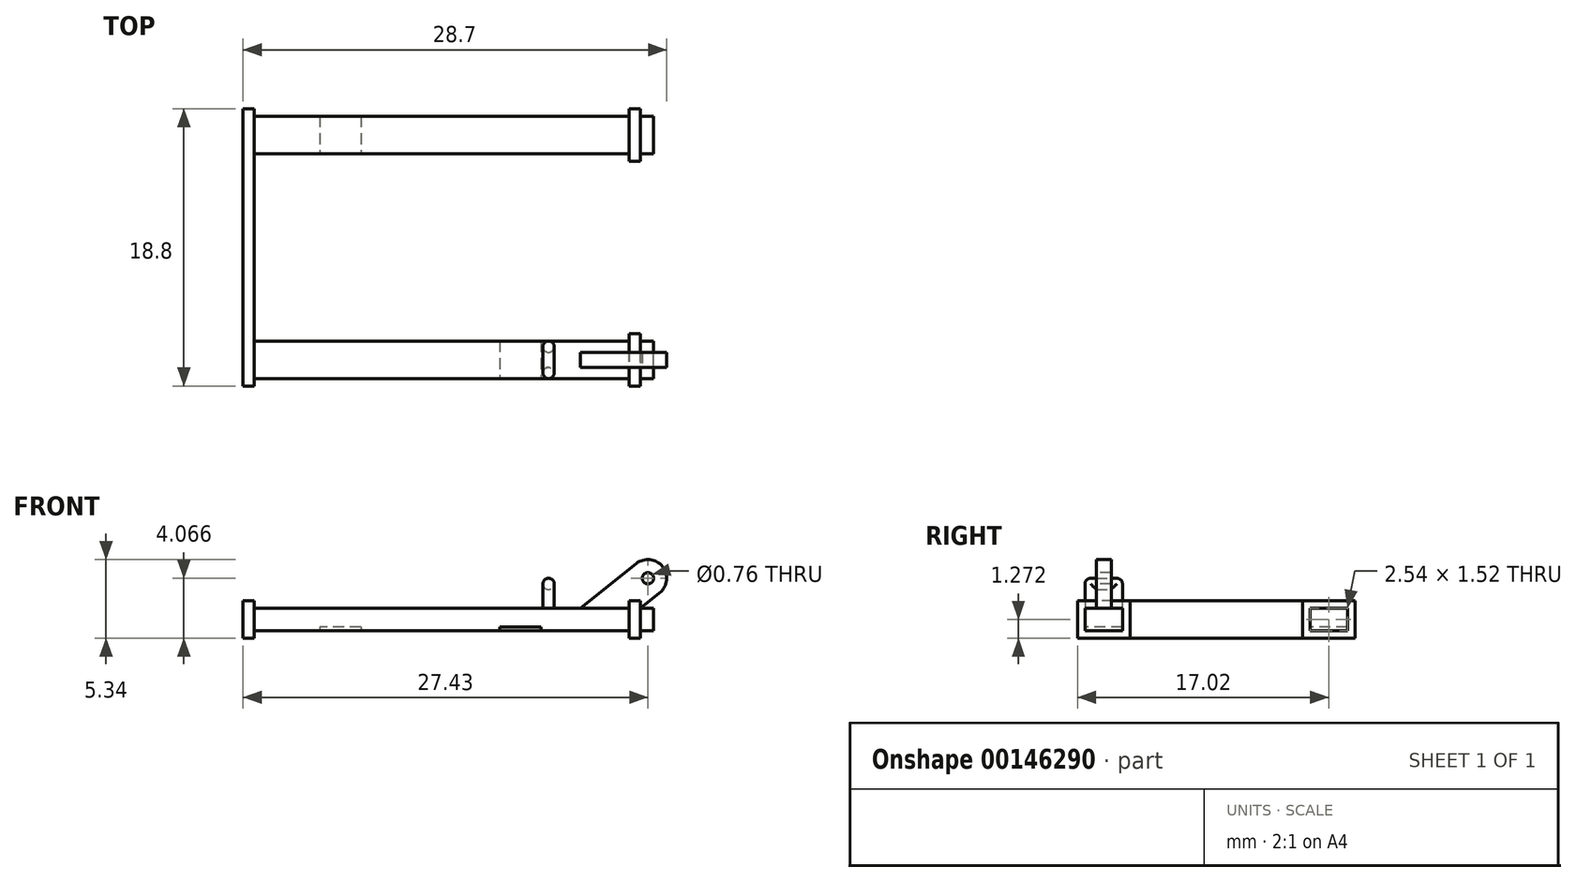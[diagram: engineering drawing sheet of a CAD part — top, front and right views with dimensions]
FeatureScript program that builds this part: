
annotation { "Feature Type Name" : "Feature", "Feature Type Description" : "" }
export const myFeature = defineFeature(function(context is Context, id is Id, definition is map)
    precondition{}
    {
        {
            var Q0;
            Q0=qCreatedBy(makeId("Top.planeOp"),FACE);
            var sketch = newSketch(context, id + "F0", { "sketchPlane" : qUnion([Q0])});
            skLineSegment(sketch, "E0.bottom", {"start": v(-12.7, 2.54) * mm, "end": v(12.7, 2.54) * mm});
            skLineSegment(sketch, "E0.top", {"start": v(-12.7, 0) * mm, "end": v(12.7, 0) * mm});
            skLineSegment(sketch, "E0.left", {"start": v(-12.7, 2.54) * mm, "end": v(-12.7, 0) * mm});
            skLineSegment(sketch, "E0.right", {"start": v(12.7, 2.54) * mm, "end": v(12.7, 0) * mm});
            skLineSegment(sketch, "E1.bottom", {"start": v(-12.7, 15.24) * mm, "end": v(12.7, 15.24) * mm});
            skLineSegment(sketch, "E1.top", {"start": v(-12.7, 17.78) * mm, "end": v(12.7, 17.78) * mm});
            skLineSegment(sketch, "E1.left", {"start": v(-12.7, 15.24) * mm, "end": v(-12.7, 17.78) * mm});
            skLineSegment(sketch, "E1.right", {"start": v(12.7, 15.24) * mm, "end": v(12.7, 17.78) * mm});
            skLineSegment(sketch, "E2.bottom", {"start": v(12.7, 18.29) * mm, "end": v(13.46, 18.29) * mm});
            skLineSegment(sketch, "E2.top", {"start": v(12.7, 14.73) * mm, "end": v(13.46, 14.73) * mm});
            skLineSegment(sketch, "E2.left", {"start": v(12.7, 18.29) * mm, "end": v(12.7, 14.73) * mm});
            skLineSegment(sketch, "E2.right", {"start": v(13.46, 18.29) * mm, "end": v(13.46, 14.73) * mm});
            skLineSegment(sketch, "E3.bottom", {"start": v(12.7, 3.05) * mm, "end": v(13.46, 3.05) * mm});
            skLineSegment(sketch, "E3.top", {"start": v(12.7, -0.5) * mm, "end": v(13.46, -0.5) * mm});
            skLineSegment(sketch, "E3.left", {"start": v(12.7, 3.05) * mm, "end": v(12.7, -0.5) * mm});
            skLineSegment(sketch, "E3.right", {"start": v(13.46, 3.05) * mm, "end": v(13.46, -0.5) * mm});
            skLineSegment(sketch, "E4.bottom", {"start": v(-12.7, 18.29) * mm, "end": v(-13.46, 18.29) * mm});
            skLineSegment(sketch, "E4.top", {"start": v(-12.7, -0.5) * mm, "end": v(-13.46, -0.5) * mm});
            skLineSegment(sketch, "E4.left", {"start": v(-12.7, 18.29) * mm, "end": v(-12.7, -0.5) * mm});
            skLineSegment(sketch, "E4.right", {"start": v(-13.46, 18.29) * mm, "end": v(-13.46, -0.5) * mm});
            skLineSegment(sketch, "E5.bottom", {"start": v(7.62, 15.24) * mm, "end": v(9.14, 15.24) * mm});
            skLineSegment(sketch, "E5.top", {"start": v(7.62, 2.54) * mm, "end": v(9.14, 2.54) * mm});
            skLineSegment(sketch, "E5.left", {"start": v(7.62, 15.24) * mm, "end": v(7.62, 2.54) * mm});
            skLineSegment(sketch, "E5.right", {"start": v(9.14, 15.24) * mm, "end": v(9.14, 2.54) * mm});
            skSolve(sketch);
        }
        {
            var Q0;
            {var subQ3=sQuery(id+"F0.wireOp",EDGE,"E1.top");Q0=makeQuery(id+"F0.imprint","IMPRINT",FACE,{"disambiguationData":[TD([[makeQuery(id+"F0.imprint","IMPRINT",EDGE,{"derivedFrom":subQ3}),-1.0]])]});}
            var Q1;
            {var subQ3=sQuery(id+"F0.wireOp",EDGE,"E4.bottom");Q1=makeQuery(id+"F0.imprint","IMPRINT",FACE,{"disambiguationData":[TD([[makeQuery(id+"F0.imprint","IMPRINT",EDGE,{"derivedFrom":subQ3}),1.0]])]});}
            var Q2;
            {var subQ3=sQuery(id+"F0.wireOp",EDGE,"E0.top");Q2=makeQuery(id+"F0.imprint","IMPRINT",FACE,{"disambiguationData":[TD([[makeQuery(id+"F0.imprint","IMPRINT",EDGE,{"derivedFrom":subQ3}),1.0]])]});}
            var Q3;
            Q3=makeQuery(id+"F0.imprint","IMPRINT",FACE,{"disambiguationData":[TD([[makeQuery(id+"F0.imprint","IMPRINT",EDGE,{"derivedFrom":sQuery(id+"F0.wireOp",EDGE,"E5.bottom")}),-1.0]])]});
            var Q4;
            {var subQ3=sQuery(id+"F0.wireOp",EDGE,"E3.bottom");Q4=makeQuery(id+"F0.imprint","IMPRINT",FACE,{"disambiguationData":[TD([[makeQuery(id+"F0.imprint","IMPRINT",EDGE,{"derivedFrom":subQ3}),-1.0]])]});}
            var Q5;
            {var subQ3=sQuery(id+"F0.wireOp",EDGE,"E2.bottom");Q5=makeQuery(id+"F0.imprint","IMPRINT",FACE,{"disambiguationData":[TD([[makeQuery(id+"F0.imprint","IMPRINT",EDGE,{"derivedFrom":subQ3}),-1.0]])]});}
            extrude(context, id + "F1", {"entities" : qUnion([Q0, Q1, Q2, Q3, Q4, Q5]), "depth" : 1.52 * mm});
        }
        {
            var Q0;
            Q0=makeQuery(id+"F1.opExtrude","CAP_FACE",FACE,{"disambiguationData":[OSD([sQuery(id+"F0.wireOp",EDGE,"E0.bottom"),sQuery(id+"F0.wireOp",EDGE,"E0.top"),sQuery(id+"F0.wireOp",EDGE,"E1.bottom"),sQuery(id+"F0.wireOp",EDGE,"E1.top"),sQuery(id+"F0.wireOp",EDGE,"E2.bottom"),sQuery(id+"F0.wireOp",EDGE,"E2.top"),sQuery(id+"F0.wireOp",EDGE,"E2.left"),sQuery(id+"F0.wireOp",EDGE,"E2.right"),sQuery(id+"F0.wireOp",EDGE,"E3.bottom"),sQuery(id+"F0.wireOp",EDGE,"E3.top"),sQuery(id+"F0.wireOp",EDGE,"E3.left"),sQuery(id+"F0.wireOp",EDGE,"E3.right"),sQuery(id+"F0.wireOp",EDGE,"E4.bottom"),sQuery(id+"F0.wireOp",EDGE,"E4.top"),sQuery(id+"F0.wireOp",EDGE,"E4.left"),sQuery(id+"F0.wireOp",EDGE,"E4.right"),sQuery(id+"F0.wireOp",EDGE,"E5.left"),sQuery(id+"F0.wireOp",EDGE,"E5.right")])],"isStart":false});
            var sketch = newSketch(context, id + "F2", { "sketchPlane" : qUnion([Q0])});
            skLineSegment(sketch, "E6.bottom", {"start": v(-13.46, 18.29) * mm, "end": v(-12.7, 18.29) * mm});
            skLineSegment(sketch, "E6.top", {"start": v(-13.46, -0.5) * mm, "end": v(-12.7, -0.5) * mm});
            skLineSegment(sketch, "E6.left", {"start": v(-13.46, 18.29) * mm, "end": v(-13.46, -0.5) * mm});
            skLineSegment(sketch, "E6.right", {"start": v(-12.7, 18.29) * mm, "end": v(-12.7, -0.5) * mm});
            skLineSegment(sketch, "E7.bottom", {"start": v(12.7, 18.29) * mm, "end": v(13.46, 18.29) * mm});
            skLineSegment(sketch, "E7.top", {"start": v(12.7, 14.73) * mm, "end": v(13.46, 14.73) * mm});
            skLineSegment(sketch, "E7.left", {"start": v(12.7, 18.29) * mm, "end": v(12.7, 14.73) * mm});
            skLineSegment(sketch, "E7.right", {"start": v(13.46, 18.29) * mm, "end": v(13.46, 14.73) * mm});
            skLineSegment(sketch, "E8.bottom", {"start": v(12.7, 3.05) * mm, "end": v(13.46, 3.05) * mm});
            skLineSegment(sketch, "E8.top", {"start": v(12.7, -0.5) * mm, "end": v(13.46, -0.5) * mm});
            skLineSegment(sketch, "E8.left", {"start": v(12.7, 3.05) * mm, "end": v(12.7, -0.5) * mm});
            skLineSegment(sketch, "E8.right", {"start": v(13.46, 3.05) * mm, "end": v(13.46, -0.5) * mm});
            skSolve(sketch);
        }
        {
            var Q0;
            Q0=qSketchRegion(id+"F2",true);
            extrude(context, id + "F3", {"entities" : qUnion([Q0]), "operationType" : NewBodyOperationType.ADD, "depth" : 0.5 * mm, "hasSecondDirection" : true, "secondDirectionOppositeDirection" : true, "secondDirectionDepth" : 2.03 * mm});
        }
        {
            var Q0;
            Q0=makeQuery(id+"F1.opExtrude","SWEPT_FACE",FACE,{"disambiguationData":[OSD([sQuery(id+"F0.wireOp",EDGE,"E0.top")])]});
            var sketch = newSketch(context, id + "F4", { "sketchPlane" : qUnion([Q0])});
            skLineSegment(sketch, "E9", {"start": v(14.76, 2.56) * mm, "end": v(13.46, 1.52) * mm});
            skArc(sketch, "E10", {"start": v(14.76, 2.56) * mm, "mid": v(14.96, 4.35) * mm, "end": v(13.18, 4.55) * mm});
            skLineSegment(sketch, "E11", {"start": v(13.18, 4.55) * mm, "end": v(9.4, 1.52) * mm});
            skLineSegment(sketch, "E12", {"start": v(9.4, 1.52) * mm, "end": v(13.46, 1.52) * mm});
            skCircle(sketch, "E13", {"center": v(13.97, 3.56) * mm, "radius": 0.38 * mm});
            skSolve(sketch);
        }
        {
            var Q0;
            Q0=qSketchRegion(id+"F4",true);
            extrude(context, id + "F5", {"entities" : qUnion([Q0]), "operationType" : NewBodyOperationType.ADD, "oppositeDirection" : true, "depth" : 1.78 * mm});
        }
        {
            var Q0;
            Q0=makeQuery(id+"F5.boolean.opBoolean","MERGE",FACE,{"derivedFrom":[makeQuery(id+"F1.opExtrude","SWEPT_FACE",FACE,{"disambiguationData":[OSD([sQuery(id+"F0.wireOp",EDGE,"E0.top")])]}),makeQuery(id+"F5.opExtrude","CAP_FACE",FACE,{"disambiguationData":[OSD([sQuery(id+"F4.wireOp",EDGE,"E9"),sQuery(id+"F4.wireOp",EDGE,"E10"),sQuery(id+"F4.wireOp",EDGE,"E11"),sQuery(id+"F4.wireOp",EDGE,"E12"),sQuery(id+"F4.wireOp",EDGE,"E13")])],"isStart":true})]});
            var sketch = newSketch(context, id + "F6", { "sketchPlane" : qUnion([Q0])});
            skLineSegment(sketch, "E14", {"start": v(9.4, 1.52) * mm, "end": v(12.7, 1.52) * mm});
            skLineSegment(sketch, "E15", {"start": v(12.7, 1.52) * mm, "end": v(12.7, 2.03) * mm});
            skLineSegment(sketch, "E16", {"start": v(12.7, 2.03) * mm, "end": v(13.46, 2.03) * mm});
            skLineSegment(sketch, "E17", {"start": v(13.46, 2.03) * mm, "end": v(13.46, 1.52) * mm});
            skLineSegment(sketch, "E18", {"start": v(13.46, 1.52) * mm, "end": v(14.76, 2.56) * mm});
            skArc(sketch, "E19", {"start": v(14.76, 2.56) * mm, "mid": v(14.96, 4.35) * mm, "end": v(13.18, 4.55) * mm});
            skLineSegment(sketch, "E20", {"start": v(9.4, 1.52) * mm, "end": v(13.18, 4.55) * mm});
            skSolve(sketch);
        }
        {
            var Q0;
            Q0=qSketchRegion(id+"F6",true);
            extrude(context, id + "F7", {"entities" : qUnion([Q0]), "operationType" : NewBodyOperationType.REMOVE, "oppositeDirection" : true, "depth" : 0.76 * mm});
        }
        {
            var Q0;
            Q0=makeQuery(id+"F5.boolean.opBoolean","MERGE",FACE,{"derivedFrom":[makeQuery(id+"F1.opExtrude","SWEPT_FACE",FACE,{"disambiguationData":[OSD([sQuery(id+"F0.wireOp",EDGE,"E0.top")])]}),makeQuery(id+"F5.opExtrude","CAP_FACE",FACE,{"disambiguationData":[OSD([sQuery(id+"F4.wireOp",EDGE,"E9"),sQuery(id+"F4.wireOp",EDGE,"E10"),sQuery(id+"F4.wireOp",EDGE,"E11"),sQuery(id+"F4.wireOp",EDGE,"E12"),sQuery(id+"F4.wireOp",EDGE,"E13")])],"isStart":true})]});
            cPlane(context, id + "F8", {"entities" : qUnion([Q0]), "cplaneType" : CPlaneType.OFFSET, "offset" : 8.9 * mm, "oppositeDirection" : true, "width" : 152.4 * mm, "height" : 152.4 * mm});
        }
        {
            var Q0;
            Q0=makeQuery(id+"F1.opExtrude","CAP_FACE",FACE,{"disambiguationData":[OSD([sQuery(id+"F0.wireOp",EDGE,"E0.bottom"),sQuery(id+"F0.wireOp",EDGE,"E0.top"),sQuery(id+"F0.wireOp",EDGE,"E1.bottom"),sQuery(id+"F0.wireOp",EDGE,"E1.top"),sQuery(id+"F0.wireOp",EDGE,"E2.bottom"),sQuery(id+"F0.wireOp",EDGE,"E2.top"),sQuery(id+"F0.wireOp",EDGE,"E2.left"),sQuery(id+"F0.wireOp",EDGE,"E2.right"),sQuery(id+"F0.wireOp",EDGE,"E3.bottom"),sQuery(id+"F0.wireOp",EDGE,"E3.top"),sQuery(id+"F0.wireOp",EDGE,"E3.left"),sQuery(id+"F0.wireOp",EDGE,"E3.right"),sQuery(id+"F0.wireOp",EDGE,"E4.bottom"),sQuery(id+"F0.wireOp",EDGE,"E4.top"),sQuery(id+"F0.wireOp",EDGE,"E4.left"),sQuery(id+"F0.wireOp",EDGE,"E4.right"),sQuery(id+"F0.wireOp",EDGE,"E5.left"),sQuery(id+"F0.wireOp",EDGE,"E5.right")])],"isStart":true});
            var sketch = newSketch(context, id + "F9", { "sketchPlane" : qUnion([Q0])});
            skLineSegment(sketch, "E21.bottom", {"start": v(6.73, -2.54) * mm, "end": v(3.94, -2.54) * mm});
            skLineSegment(sketch, "E21.top", {"start": v(6.73, 0) * mm, "end": v(3.94, 0) * mm});
            skLineSegment(sketch, "E21.left", {"start": v(6.73, -2.54) * mm, "end": v(6.73, 0) * mm});
            skLineSegment(sketch, "E21.right", {"start": v(3.94, -2.54) * mm, "end": v(3.94, 0) * mm});
            skLineSegment(sketch, "E22.bottom", {"start": v(-5.46, -17.78) * mm, "end": v(-8.26, -17.78) * mm});
            skLineSegment(sketch, "E22.top", {"start": v(-5.46, -15.24) * mm, "end": v(-8.26, -15.24) * mm});
            skLineSegment(sketch, "E22.left", {"start": v(-5.46, -17.78) * mm, "end": v(-5.46, -15.24) * mm});
            skLineSegment(sketch, "E22.right", {"start": v(-8.26, -17.78) * mm, "end": v(-8.26, -15.24) * mm});
            skSolve(sketch);
        }
        {
            var Q0;
            Q0 = qSketchRegion(id + "F9", true);
            extrude(context, id + "F10", {"entities" : qUnion([Q0]), "operationType" : NewBodyOperationType.REMOVE, "oppositeDirection" : true, "depth" : 0.25 * mm});
        }
        {
            var Q0;
            Q0=makeQuery(id+"F7.boolean.opBoolean","MERGE",FACE,{"derivedFrom":[makeQuery(id+"F3.boolean.opBoolean","MERGE",FACE,{"derivedFrom":[makeQuery(id+"F1.opExtrude","SWEPT_FACE",FACE,{"disambiguationData":[OSD([sQuery(id+"F0.wireOp",EDGE,"E3.right")])]}),makeQuery(id+"F3.opExtrude","SWEPT_FACE",FACE,{"disambiguationData":[OSD([sQuery(id+"F2.wireOp",EDGE,"E8.right")])]})]}),makeQuery(id+"F7.opExtrude","SWEPT_FACE",FACE,{"disambiguationData":[OSD([sQuery(id+"F6.wireOp",EDGE,"E17")])]})]});
            var sketch = newSketch(context, id + "F11", { "sketchPlane" : qUnion([Q0])});
            skLineSegment(sketch, "E23.bottom", {"start": v(0, 1.52) * mm, "end": v(2.54, 1.52) * mm});
            skLineSegment(sketch, "E23.top", {"start": v(0, 0) * mm, "end": v(2.54, 0) * mm});
            skLineSegment(sketch, "E23.left", {"start": v(0, 1.52) * mm, "end": v(0, 0) * mm});
            skLineSegment(sketch, "E23.right", {"start": v(2.54, 1.52) * mm, "end": v(2.54, 0) * mm});
            skSolve(sketch);
        }
        {
            var Q0;
            Q0 = qSketchRegion(id + "F11", true);
            extrude(context, id + "F12", {"entities" : qUnion([Q0]), "operationType" : NewBodyOperationType.ADD, "depth" : 0.89 * mm});
        }
        {
            var Q0;
            Q0=makeQuery(id+"FbFiRezVOLwQmsc_1.1.F7.boolean.opBoolean","MERGE",FACE,{"derivedFrom":[makeQuery(id+"F3.boolean.opBoolean","MERGE",FACE,{"derivedFrom":[makeQuery(id+"F1.opExtrude","SWEPT_FACE",FACE,{"disambiguationData":[OSD([sQuery(id+"F0.wireOp",EDGE,"E2.right")])]}),makeQuery(id+"F3.opExtrude","SWEPT_FACE",FACE,{"disambiguationData":[OSD([sQuery(id+"F2.wireOp",EDGE,"E7.right")])]})]}),makeQuery(id+"FbFiRezVOLwQmsc_1.1.F7.opExtrude","SWEPT_FACE",FACE,{"disambiguationData":[OSD([sQuery(id+"F6.wireOp",EDGE,"E17")])]})]});
            var sketch = newSketch(context, id + "F13", { "sketchPlane" : qUnion([Q0])});
            skLineSegment(sketch, "E24.bottom", {"start": v(15.24, 1.52) * mm, "end": v(17.78, 1.52) * mm});
            skLineSegment(sketch, "E24.top", {"start": v(15.24, 0) * mm, "end": v(17.78, 0) * mm});
            skLineSegment(sketch, "E24.left", {"start": v(15.24, 1.52) * mm, "end": v(15.24, 0) * mm});
            skLineSegment(sketch, "E24.right", {"start": v(17.78, 1.52) * mm, "end": v(17.78, 0) * mm});
            skSolve(sketch);
        }
        {
            var Q0;
            Q0 = qSketchRegion(id + "F13", true);
            extrude(context, id + "F14", {"entities" : qUnion([Q0]), "operationType" : NewBodyOperationType.ADD, "depth" : 0.89 * mm});
        }
        {
            var Q0;
            {var subQ0=sQuery(id+"F6.wireOp",EDGE,"E14");Q0=makeQuery(id+"FbFiRezVOLwQmsc_1.1.F7.boolean.opBoolean","MERGE",FACE,{"derivedFrom":[makeQuery(id+"F7.boolean.opBoolean","MERGE",FACE,{"derivedFrom":[makeQuery(id+"F1.opExtrude","CAP_FACE",FACE,{"disambiguationData":[OSD([sQuery(id+"F0.wireOp",EDGE,"E0.bottom"),sQuery(id+"F0.wireOp",EDGE,"E0.top"),sQuery(id+"F0.wireOp",EDGE,"E1.bottom"),sQuery(id+"F0.wireOp",EDGE,"E1.top"),sQuery(id+"F0.wireOp",EDGE,"E2.bottom"),sQuery(id+"F0.wireOp",EDGE,"E2.top"),sQuery(id+"F0.wireOp",EDGE,"E2.left"),sQuery(id+"F0.wireOp",EDGE,"E2.right"),sQuery(id+"F0.wireOp",EDGE,"E3.bottom"),sQuery(id+"F0.wireOp",EDGE,"E3.top"),sQuery(id+"F0.wireOp",EDGE,"E3.left"),sQuery(id+"F0.wireOp",EDGE,"E3.right"),sQuery(id+"F0.wireOp",EDGE,"E4.bottom"),sQuery(id+"F0.wireOp",EDGE,"E4.top"),sQuery(id+"F0.wireOp",EDGE,"E4.left"),sQuery(id+"F0.wireOp",EDGE,"E4.right"),sQuery(id+"F0.wireOp",EDGE,"E5.left"),sQuery(id+"F0.wireOp",EDGE,"E5.right")])],"isStart":false}),makeQuery(id+"F7.opExtrude","SWEPT_FACE",FACE,{"disambiguationData":[OSD([subQ0])]})]}),makeQuery(id+"FbFiRezVOLwQmsc_1.1.F7.opExtrude","SWEPT_FACE",FACE,{"disambiguationData":[OSD([subQ0])]})]});}
            var sketch = newSketch(context, id + "F15", { "sketchPlane" : qUnion([Q0])});
            skLineSegment(sketch, "E25.bottom", {"start": v(7.62, 2.54) * mm, "end": v(6.86, 2.54) * mm});
            skLineSegment(sketch, "E25.top", {"start": v(7.62, 1.78) * mm, "end": v(6.86, 1.78) * mm});
            skLineSegment(sketch, "E25.left", {"start": v(7.62, 2.54) * mm, "end": v(7.62, 1.78) * mm});
            skLineSegment(sketch, "E25.right", {"start": v(6.86, 2.54) * mm, "end": v(6.86, 1.78) * mm});
            skLineSegment(sketch, "E26.bottom", {"start": v(7.62, 0) * mm, "end": v(6.86, 0) * mm});
            skLineSegment(sketch, "E26.top", {"start": v(7.62, 0.76) * mm, "end": v(6.86, 0.76) * mm});
            skLineSegment(sketch, "E26.left", {"start": v(7.62, 0) * mm, "end": v(7.62, 0.76) * mm});
            skLineSegment(sketch, "E26.right", {"start": v(6.86, 0) * mm, "end": v(6.86, 0.76) * mm});
            skSolve(sketch);
        }
        {
            var Q0;
            Q0 = qSketchRegion(id + "F15", true);
            extrude(context, id + "F16", {"entities" : qUnion([Q0]), "operationType" : NewBodyOperationType.ADD, "depth" : 2.03 * mm});
        }
        {
            var Q0;
            Q0=makeQuery(id+"F16.opExtrude","SWEPT_FACE",FACE,{"disambiguationData":[OSD([sQuery(id+"F15.wireOp",EDGE,"E25.top")])]});
            var sketch = newSketch(context, id + "F17", { "sketchPlane" : qUnion([Q0])});
            skLineSegment(sketch, "E27.bottom", {"start": v(6.86, 3.56) * mm, "end": v(7.62, 3.56) * mm});
            skLineSegment(sketch, "E27.top", {"start": v(6.86, 2.8) * mm, "end": v(7.62, 2.8) * mm});
            skLineSegment(sketch, "E27.left", {"start": v(6.86, 3.56) * mm, "end": v(6.86, 2.8) * mm});
            skLineSegment(sketch, "E27.right", {"start": v(7.62, 3.56) * mm, "end": v(7.62, 2.8) * mm});
            skSolve(sketch);
        }
        {
            var Q0;
            Q0 = qSketchRegion(id + "F17", true);
            var Q1;
            Q1=makeQuery(id+"F16.opExtrude","SWEPT_FACE",FACE,{"disambiguationData":[OSD([sQuery(id+"F15.wireOp",EDGE,"E26.top")])]});
            extrude(context, id + "F18", {"entities" : qUnion([Q0]), "operationType" : NewBodyOperationType.ADD, "endBound" : BoundingType.UP_TO_SURFACE, "endBoundEntityFace" : qUnion([Q1]), "depth" : 25.4 * mm});
        }
        {
            var Q0;
            Q0=makeQuery(id+"F16.opExtrude","SWEPT_EDGE",EDGE,{"disambiguationData":[OSD([sQuery(id+"F0.wireOp",EDGE,"E0.bottom"),sQuery(id+"F15.wireOp",EDGE,"E25.bottom"),sQuery(id+"F15.wireOp",EDGE,"E25.right")])]});
            var Q1;
            Q1=makeQuery(id+"F16.opExtrude","SWEPT_EDGE",EDGE,{"disambiguationData":[OSD([sQuery(id+"F0.wireOp",EDGE,"E5.left"),sQuery(id+"F15.wireOp",EDGE,"E25.bottom"),sQuery(id+"F15.wireOp",EDGE,"E25.left")])]});
            var Q2;
            Q2=makeQuery(id+"F16.opExtrude","CAP_EDGE",EDGE,{"disambiguationData":[OSD([sQuery(id+"F15.wireOp",EDGE,"E25.bottom")])],"isStart":false});
            var Q3;
            Q3=makeQuery(id+"F18.boolean.opBoolean","MERGE",EDGE,{"derivedFrom":[makeQuery(id+"F16.opExtrude","CAP_EDGE",EDGE,{"disambiguationData":[OSD([sQuery(id+"F15.wireOp",EDGE,"E25.left")])],"isStart":false}),makeQuery(id+"F16.opExtrude","CAP_EDGE",EDGE,{"disambiguationData":[OSD([sQuery(id+"F15.wireOp",EDGE,"E26.left")])],"isStart":false}),makeQuery(id+"F18.opExtrude","SWEPT_EDGE",EDGE,{"disambiguationData":[OSD([sQuery(id+"F17.wireOp",EDGE,"E27.bottom"),sQuery(id+"F17.wireOp",EDGE,"E27.right")])]})]});
            var Q4;
            Q4=makeQuery(id+"F18.boolean.opBoolean","MERGE",EDGE,{"derivedFrom":[makeQuery(id+"F16.opExtrude","CAP_EDGE",EDGE,{"disambiguationData":[OSD([sQuery(id+"F15.wireOp",EDGE,"E25.right")])],"isStart":false}),makeQuery(id+"F16.opExtrude","CAP_EDGE",EDGE,{"disambiguationData":[OSD([sQuery(id+"F15.wireOp",EDGE,"E26.right")])],"isStart":false}),makeQuery(id+"F18.opExtrude","SWEPT_EDGE",EDGE,{"disambiguationData":[OSD([sQuery(id+"F17.wireOp",EDGE,"E27.bottom"),sQuery(id+"F17.wireOp",EDGE,"E27.left")])]})]});
            var Q5;
            Q5=makeQuery(id+"F18.opExtrude","SWEPT_EDGE",EDGE,{"disambiguationData":[OSD([sQuery(id+"F15.wireOp",EDGE,"E25.top"),sQuery(id+"F15.wireOp",EDGE,"E25.right"),sQuery(id+"F17.wireOp",EDGE,"E27.top"),sQuery(id+"F17.wireOp",EDGE,"E27.left")])]});
            var Q6;
            Q6=makeQuery(id+"F16.opExtrude","SWEPT_EDGE",EDGE,{"disambiguationData":[OSD([sQuery(id+"F15.wireOp",EDGE,"E25.top"),sQuery(id+"F15.wireOp",EDGE,"E25.right")])]});
            var Q7;
            Q7=makeQuery(id+"F16.opExtrude","SWEPT_EDGE",EDGE,{"disambiguationData":[OSD([sQuery(id+"F15.wireOp",EDGE,"E26.top"),sQuery(id+"F15.wireOp",EDGE,"E26.right")])]});
            var Q8;
            Q8=makeQuery(id+"F16.opExtrude","SWEPT_EDGE",EDGE,{"disambiguationData":[OSD([sQuery(id+"F15.wireOp",EDGE,"E26.top"),sQuery(id+"F15.wireOp",EDGE,"E26.left")])]});
            var Q9;
            Q9=makeQuery(id+"F16.opExtrude","SWEPT_EDGE",EDGE,{"disambiguationData":[OSD([sQuery(id+"F0.wireOp",EDGE,"E0.top"),sQuery(id+"F6.wireOp",EDGE,"E14"),sQuery(id+"F15.wireOp",EDGE,"E26.bottom"),sQuery(id+"F15.wireOp",EDGE,"E26.right")])]});
            var Q10;
            Q10=makeQuery(id+"F16.opExtrude","CAP_EDGE",EDGE,{"disambiguationData":[OSD([sQuery(id+"F15.wireOp",EDGE,"E26.bottom")])],"isStart":false});
            var Q11;
            Q11=makeQuery(id+"F18.opExtrude","SWEPT_EDGE",EDGE,{"disambiguationData":[OSD([sQuery(id+"F15.wireOp",EDGE,"E25.top"),sQuery(id+"F15.wireOp",EDGE,"E25.left"),sQuery(id+"F17.wireOp",EDGE,"E27.top"),sQuery(id+"F17.wireOp",EDGE,"E27.right")])]});
            var Q12;
            Q12=makeQuery(id+"F16.opExtrude","SWEPT_EDGE",EDGE,{"disambiguationData":[OSD([sQuery(id+"F0.wireOp",EDGE,"E0.top"),sQuery(id+"F6.wireOp",EDGE,"E14"),sQuery(id+"F15.wireOp",EDGE,"E26.bottom"),sQuery(id+"F15.wireOp",EDGE,"E26.left")])]});
            var Q13;
            Q13=makeQuery(id+"F16.opExtrude","SWEPT_EDGE",EDGE,{"disambiguationData":[OSD([sQuery(id+"F15.wireOp",EDGE,"E25.top"),sQuery(id+"F15.wireOp",EDGE,"E25.left")])]});
            fillet(context, id + "F19", {"entities" : qUnion([Q0, Q1, Q2, Q3, Q4, Q5, Q6, Q7, Q8, Q9, Q10, Q11, Q12, Q13]), "radius" : 0.38 * mm, "tangentPropagation" : true, "allowEdgeOverflow" : false});
        }
    });
